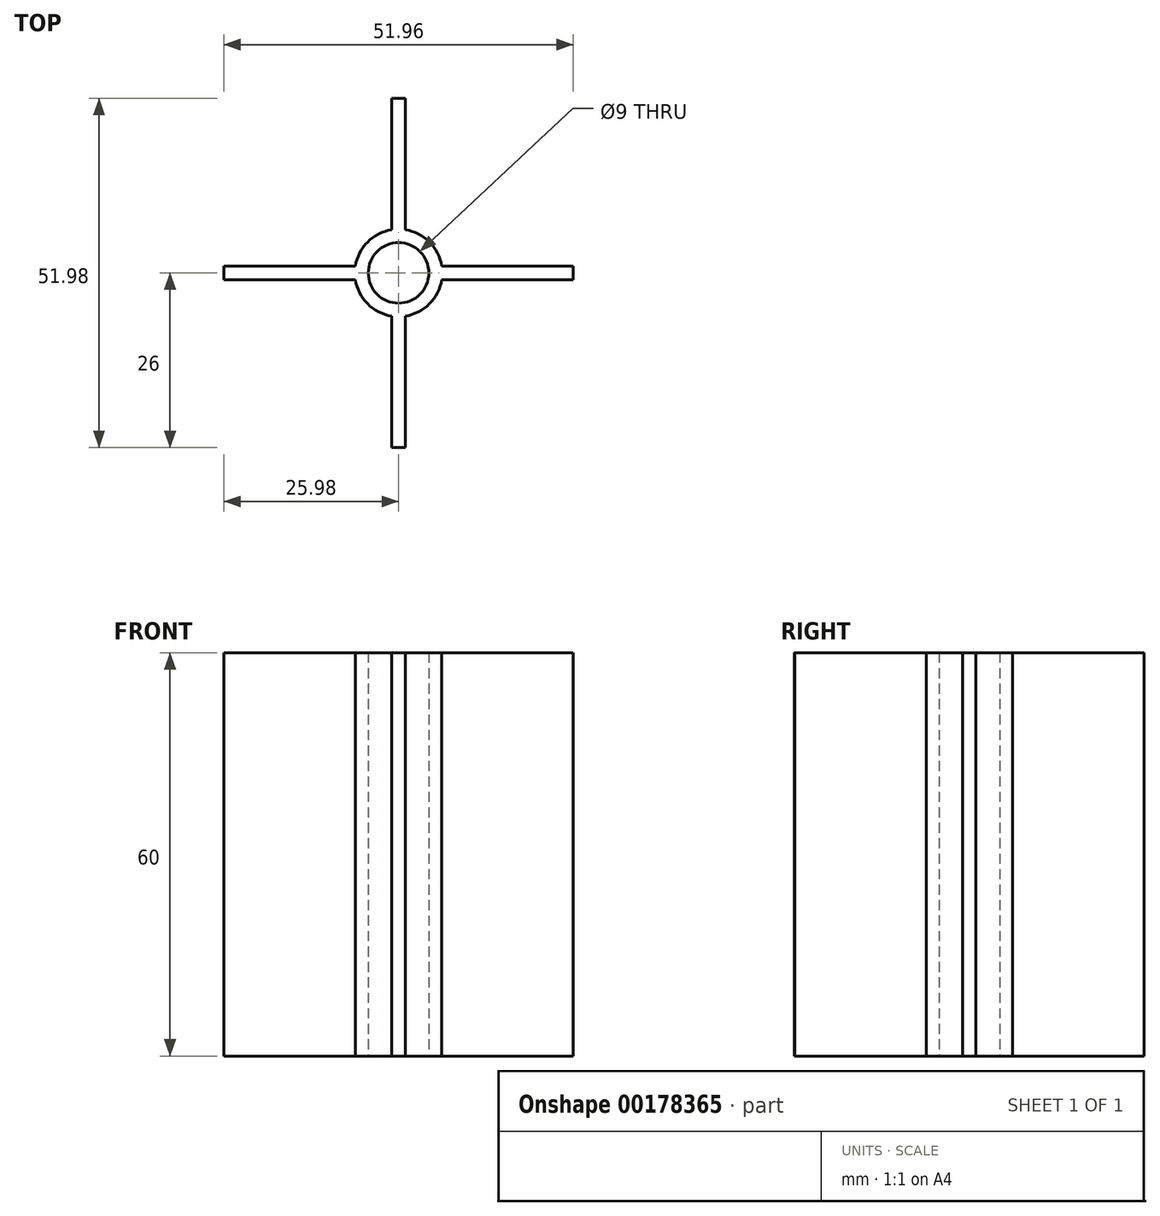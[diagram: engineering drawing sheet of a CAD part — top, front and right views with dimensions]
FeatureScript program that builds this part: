
annotation { "Feature Type Name" : "Feature", "Feature Type Description" : "" }
export const myFeature = defineFeature(function(context is Context, id is Id, definition is map)
    precondition{}
    {
        {
            var Q0;
            Q0=qCreatedBy(makeId("Top.planeOp"),FACE);
            var sketch = newSketch(context, id + "F0", { "sketchPlane" : qUnion([Q0])});
            skCircle(sketch, "E0", {"center": v(0, 0) * mm, "radius": 4.5 * mm});
            skCircle(sketch, "E1", {"center": v(0, 0) * mm, "radius": 26 * mm});
            skCircle(sketch, "E2", {"center": v(0, 0) * mm, "radius": 6.5 * mm});
            skLineSegment(sketch, "E3.top", {"start": v(1, 25.98) * mm, "end": v(-1, 25.98) * mm});
            skLineSegment(sketch, "E3.left", {"start": v(1, 6.42) * mm, "end": v(1, 25.98) * mm});
            skLineSegment(sketch, "E3.right", {"start": v(-1, 6.42) * mm, "end": v(-1, 25.98) * mm});
            skPoint(sketch, "E3.middle", {"position": v(0, 16.2) * mm});
            skLineSegment(sketch, "E4.bottom", {"start": v(6.42, -1) * mm, "end": v(25.98, -1) * mm});
            skLineSegment(sketch, "E4.top", {"start": v(6.42, 1) * mm, "end": v(25.98, 1) * mm});
            skLineSegment(sketch, "E4.right", {"start": v(25.98, -1) * mm, "end": v(25.98, 1) * mm});
            skPoint(sketch, "E4.middle", {"position": v(16.2, 0) * mm});
            skLineSegment(sketch, "E5.left", {"start": v(1, -6.42) * mm, "end": v(1, -25.98) * mm});
            skLineSegment(sketch, "E5.right", {"start": v(-1, -6.42) * mm, "end": v(-1, -25.98) * mm});
            skPoint(sketch, "E5.middle", {"position": v(0, -16.2) * mm});
            skLineSegment(sketch, "E6.bottom", {"start": v(-6.42, -1) * mm, "end": v(-25.98, -1) * mm});
            skLineSegment(sketch, "E6.top", {"start": v(-6.42, 1) * mm, "end": v(-25.98, 1) * mm});
            skLineSegment(sketch, "E6.right", {"start": v(-25.98, -1) * mm, "end": v(-25.98, 1) * mm});
            skPoint(sketch, "E6.middle", {"position": v(-16.2, 0) * mm});
            skSolve(sketch);
        }
        {
            var Q0;
            Q0=makeQuery(id+"F0.imprint","IMPRINT",FACE,{"disambiguationData":[TD([[makeQuery(id+"F0.imprint","IMPRINT",EDGE,{"derivedFrom":sQuery(id+"F0.wireOp",EDGE,"E0")}),-1.0]])]});
            var Q1;
            {var subQ0=sQuery(id+"F0.wireOp",EDGE,"E6.bottom");Q1=makeQuery(id+"F0.imprint","IMPRINT",FACE,{"disambiguationData":[TD([[makeQuery(id+"F0.imprint","IMPRINT",EDGE,{"derivedFrom":subQ0}),-1.0]])]});}
            var Q2;
            {var subQ0=sQuery(id+"F0.wireOp",EDGE,"E5.left");Q2=makeQuery(id+"F0.imprint","IMPRINT",FACE,{"disambiguationData":[TD([[makeQuery(id+"F0.imprint","IMPRINT",EDGE,{"derivedFrom":subQ0}),-1.0]])]});}
            var Q3;
            {var subQ0=sQuery(id+"F0.wireOp",EDGE,"E4.bottom");Q3=makeQuery(id+"F0.imprint","IMPRINT",FACE,{"disambiguationData":[TD([[makeQuery(id+"F0.imprint","IMPRINT",EDGE,{"derivedFrom":subQ0}),1.0]])]});}
            var Q4;
            Q4=makeQuery(id+"F0.imprint","IMPRINT",FACE,{"disambiguationData":[TD([[makeQuery(id+"F0.imprint","IMPRINT",EDGE,{"derivedFrom":sQuery(id+"F0.wireOp",EDGE,"E3.top")}),1.0]])]});
            extrude(context, id + "F1", {"entities" : qUnion([Q0, Q1, Q2, Q3, Q4]), "depth" : 60 * mm});
        }
    });
